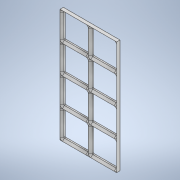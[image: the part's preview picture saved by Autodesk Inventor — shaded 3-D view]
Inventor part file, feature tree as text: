
AUTODESK INVENTOR PART (.ipt)
format: ipt  version: 2021 (Build 250183000, 183)  size: 226,816 bytes
history: native  units: mm
features: extrude x2, chamfer x1, pattern_linear x1, sketch x1
ambient origin geometry x8: Origin, YZ Plane, XZ Plane, XY Plane, X Axis, Y Axis, Z Axis, Center Point
bodies: Solid1 (feature_tree)
feature tree (5):
  extrude  "Extrusion1"  TaperAngle=0.0deg  [1 undecoded]
  extrude  "Extrusion2"  Depth=42.0mm
  chamfer  "Chamfer2"  Distance=42.0mm
  pattern_linear  "Rectangular Pattern1"  Spacing1=2.846mm  [1 undecoded]
  sketch  "Sketch1"  dims[d1=0.0mm d2=0.0mm d3=0.0mm d7=42.0mm d8=42.0mm d9=2.846mm d10=1.6mm d11=1.6mm d12=1.6mm d13=1.6mm d14=2.846mm d15=2.0mm d16=45.0deg d17=20.0mm d19=42.0mm d20=40.0mm d22=42.0mm]
note: 2 required parameter values undecoded (feature->parameter linkage not recoverable at this tier; creation-order binding heuristic only, values carry confidence <= 0.55)
